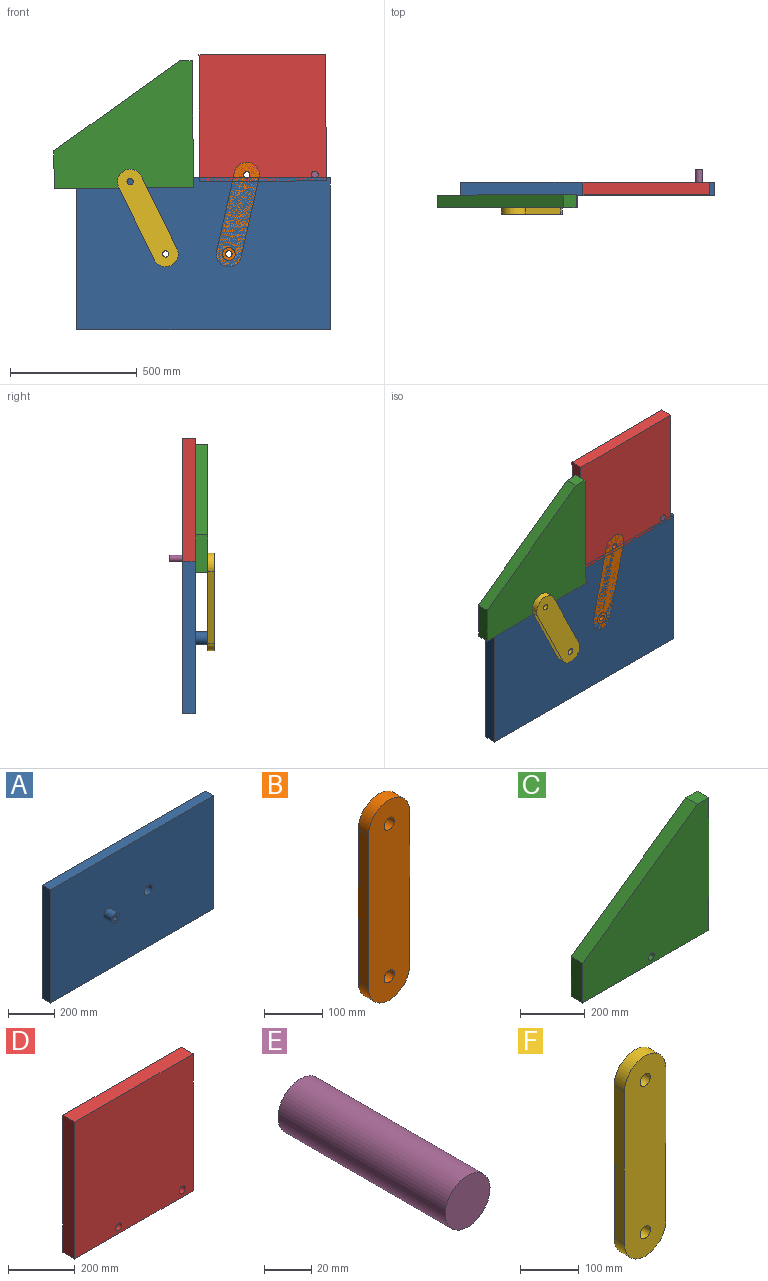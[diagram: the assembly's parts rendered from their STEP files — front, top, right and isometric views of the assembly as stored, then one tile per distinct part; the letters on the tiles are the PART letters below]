
ASSEMBLY  parts=6 mates=5
PART A: 10 faces, bbox 1000x100x600 mm
  f0: plane 1000x50mm, normal (0,0,1), area 50000mm2, adj f1,f3,f6,f7
  f1: plane 600x50mm, normal (-1,0,0), area 30000mm2, adj f0,f2,f6,f7
  f2: plane 1000x50mm, normal (0,0,-1), area 50000mm2, adj f1,f3,f6,f7
  f3: plane 600x50mm, normal (1,0,0), area 30000mm2, adj f0,f2,f6,f7
  f4: cylinder r=25mm len=50mm, axis (0,-1,0), area 7854mm2, adj f6,f7
  f5: cylinder r=12.5mm len=100mm, axis (0,-1,0), area 7854mm2, adj f6,f9
  f6: plane 1000x600mm, normal (0,1,0), area 597545.6mm2, adj f0,f1,f2,f3,f4,f5
  f7: plane 1000x600mm, normal (0,-1,0), area 596073mm2, adj f0,f1,f2,f3,f4,f8
  f8: cylinder r=25mm len=50mm, axis (0,1,0), area 7854mm2, adj f7,f9
  f9: plane 50x50mm, normal (0,-1,0), area 1472.6mm2, adj f5,f8
PART B: 8 faces, bbox 100x25x420 mm
  f0: plane 320x25mm, normal (-1,0,0), area 8000mm2, adj f1,f5,f6,f7
  f1: cylinder r=50mm len=100mm, axis (0,1,0), area 3927mm2, adj f0,f2,f6,f7
  f2: plane 320x25mm, normal (1,0,0), area 8000mm2, adj f1,f5,f6,f7
  f3: cylinder r=12.5mm len=25mm, axis (0,1,0), area 1963.5mm2, adj f6,f7
  f4: cylinder r=12.5mm len=25mm, axis (0,1,0), area 1963.5mm2, adj f6,f7
  f5: cylinder r=50mm len=100mm, axis (0,1,0), area 3927mm2, adj f0,f2,f6,f7
  f6: plane 420x100mm, normal (0,-1,0), area 38872.2mm2, adj f0,f1,f2,f3,f4,f5
  f7: plane 420x100mm, normal (0,1,0), area 38872.2mm2, adj f0,f1,f2,f3,f4,f5
PART C: 10 faces, bbox 550x100x500 mm
  f0: plane 550x50mm, normal (0,0,-1), area 27500mm2, adj f1,f4,f6,f7
  f1: plane 500x50mm, normal (1,0,0), area 25000mm2, adj f0,f2,f6,f7
  f2: plane 50x50mm, normal (0,0,1), area 2500mm2, adj f1,f3,f6,f7
  f3: plane 500x350mm, normal (-0.57,0,0.82), area 30516.4mm2, adj f2,f4,f6,f7
  f4: plane 150x50mm, normal (-1,0,0), area 7500mm2, adj f0,f3,f6,f7
  f5: cylinder r=12.5mm len=50mm, axis (0,1,0), area 3927mm2, adj f6,f7
  f6: plane 550x500mm, normal (0,-1,0), area 187009.1mm2, adj f0,f1,f2,f3,f4,f5
  f7: plane 550x500mm, normal (0,1,0), area 186518.3mm2, adj f0,f1,f2,f3,f4,f5,f8
  f8: cylinder r=12.5mm len=50mm, axis (0,1,0), area 3927mm2, adj f7,f9
  f9: plane 25x25mm, normal (0,1,0), area 490.9mm2, adj f8
PART D: 8 faces, bbox 500x50x500.6 mm
  f0: plane 500.55x50mm, normal (-1,0,0), area 25027.7mm2, adj f1,f4,f6,f7
  f1: plane 500x50mm, normal (0,0,-1), area 25000mm2, adj f0,f2,f6,f7
  f2: plane 500.55x50mm, normal (1,0,0), area 25027.7mm2, adj f1,f4,f6,f7
  f3: cylinder r=13.36mm len=50mm, axis (0,1,0), area 4195.7mm2, adj f6,f7
  f4: plane 500x50mm, normal (0,0,1), area 25000mm2, adj f0,f2,f6,f7
  f5: cylinder r=12.5mm len=50mm, axis (0,1,0), area 3927mm2, adj f6,f7
  f6: plane 500.55x500mm, normal (0,-1,0), area 249225.5mm2, adj f0,f1,f2,f3,f4,f5
  f7: plane 500.55x500mm, normal (0,1,0), area 249225.5mm2, adj f0,f1,f2,f3,f4,f5
PART E: 3 faces, bbox 26.7x100x26.7 mm
  f0: cylinder r=13.36mm len=100mm, axis (0,1,0), area 8391.3mm2, adj f1,f2
  f1: plane 26.71x26.71mm, normal (0,-1,0), area 560.3mm2, adj f0
  f2: plane 26.71x26.71mm, normal (0,1,0), area 560.3mm2, adj f0
PART F: 8 faces, bbox 100x25x417.5 mm
  f0: plane 317.5x25mm, normal (-1,0,0), area 7937.5mm2, adj f1,f5,f6,f7
  f1: cylinder r=50mm len=100mm, axis (0,1,0), area 3927mm2, adj f0,f2,f6,f7
  f2: plane 317.5x25mm, normal (1,0,0), area 7937.5mm2, adj f1,f5,f6,f7
  f3: cylinder r=12.5mm len=25mm, axis (0,1,0), area 1963.5mm2, adj f6,f7
  f4: cylinder r=12.5mm len=25mm, axis (0,1,0), area 1963.5mm2, adj f6,f7
  f5: cylinder r=50mm len=100mm, axis (0,1,0), area 3927mm2, adj f0,f2,f6,f7
  f6: plane 417.5x100mm, normal (0,-1,0), area 38622.2mm2, adj f0,f1,f2,f3,f4,f5
  f7: plane 417.5x100mm, normal (0,1,0), area 38622.2mm2, adj f0,f1,f2,f3,f4,f5
PLACE A t=(-500,0,0)mm
PLACE B rot(axis=(0,1,0),12.8deg) t=(1578.36,25,-1047.14)mm
PLACE C rot(axis=(0,-1,0),0.6deg) t=(-33.92,0,-712.23)mm
PLACE D rot(axis=(0,-1,0),0.3deg) t=(-509.06,50,-796.15)mm
PLACE E rot(axis=(0,-1,0),0.3deg) t=(-509.06,50,-796.15)mm
PLACE F rot(axis=(0,-1,0),26.1deg) t=(716.59,-50,842.17)mm
MATE revolute A.f5 <-> F.f1  axis (0,-1,0) through (-650,-50,300)mm
MATE revolute F.f4 <-> C.f5  axis (0,1,0) through (-789.77,-50,585.08)mm
MATE revolute B.f3 <-> D.f5  axis (0,-1,0) through (-329.27,0,612.09)mm
MATE revolute B.f1 <-> A.f4  axis (0,-1,0) through (-400,0,300)mm
MATE fastened E.f0 <-> D.f3  axis (0,-1,0) through (-60.51,0,613.36)mm
